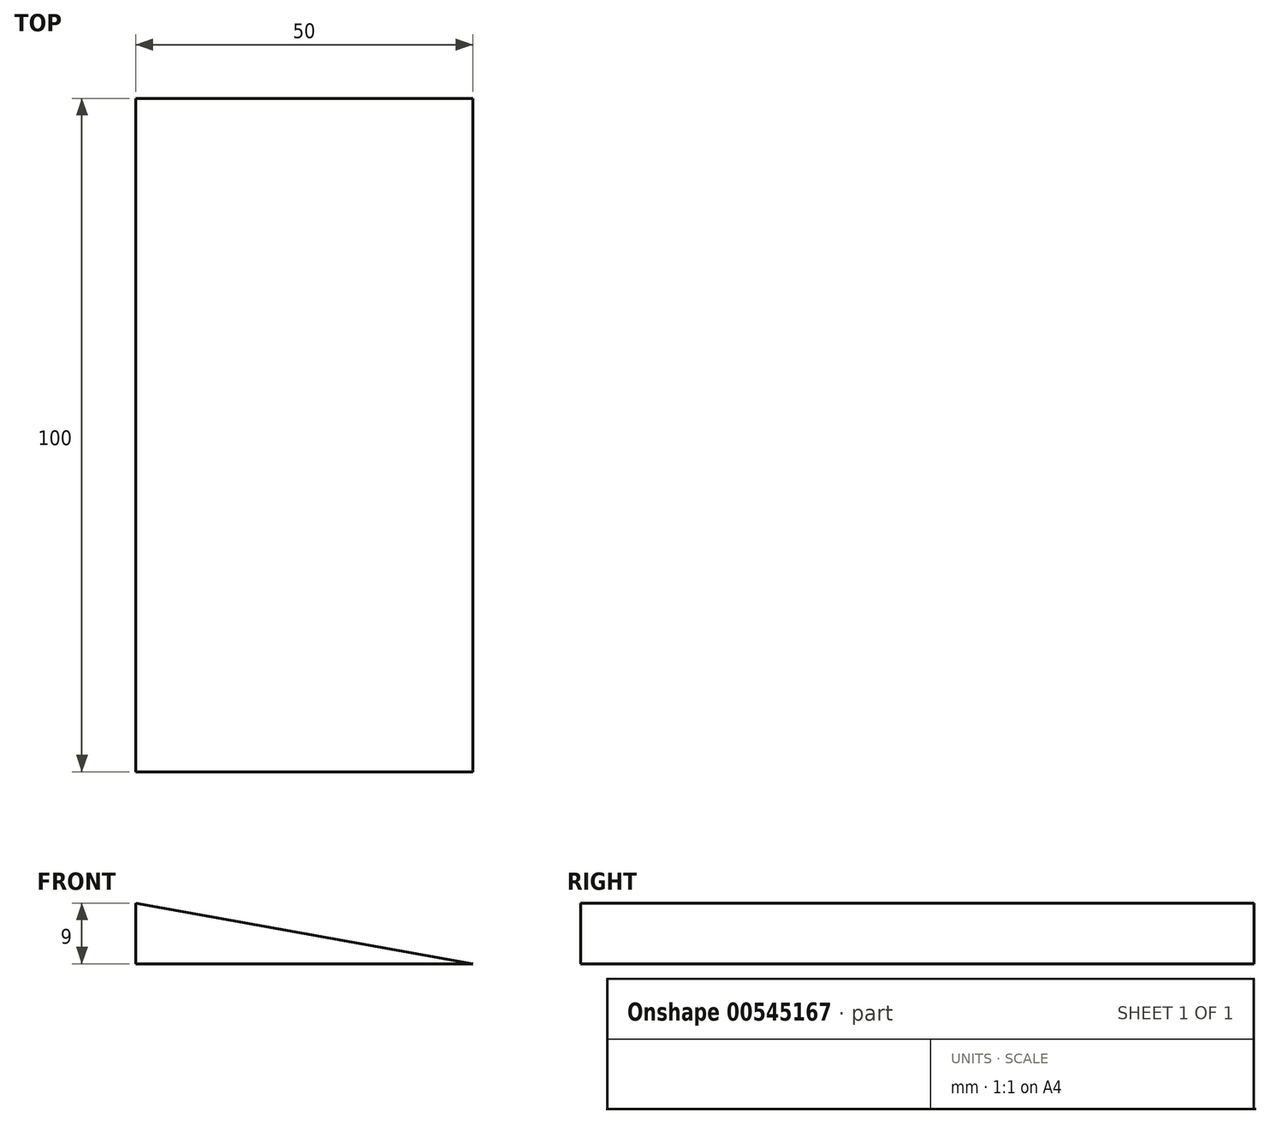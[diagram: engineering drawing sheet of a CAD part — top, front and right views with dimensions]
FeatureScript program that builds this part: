
annotation { "Feature Type Name" : "Feature", "Feature Type Description" : "" }
export const myFeature = defineFeature(function(context is Context, id is Id, definition is map)
    precondition{}
    {
        {
            var Q0;
            Q0=qCreatedBy(makeId("Front.planeOp"),FACE);
            var sketch = newSketch(context, id + "F0", { "sketchPlane" : qUnion([Q0])});
            skLineSegment(sketch, "E0", {"start": v(0, 0) * mm, "end": v(0, 9) * mm});
            skLineSegment(sketch, "E1", {"start": v(0, 9) * mm, "end": v(50, 0) * mm});
            skLineSegment(sketch, "E2", {"start": v(50, 0) * mm, "end": v(0, 0) * mm});
            skSolve(sketch);
        }
        {
            var Q0;
            Q0=makeQuery(id+"F0.imprint","IMPRINT",FACE,{"disambiguationData":[TD([[makeQuery(id+"F0.imprint","IMPRINT",EDGE,{"derivedFrom":sQuery(id+"F0.wireOp",EDGE,"E0")}),-1.0]])]});
            extrude(context, id + "F1", {"entities" : qUnion([Q0]), "depth" : 100 * mm, "offsetDistance" : 25 * mm});
        }
    });
